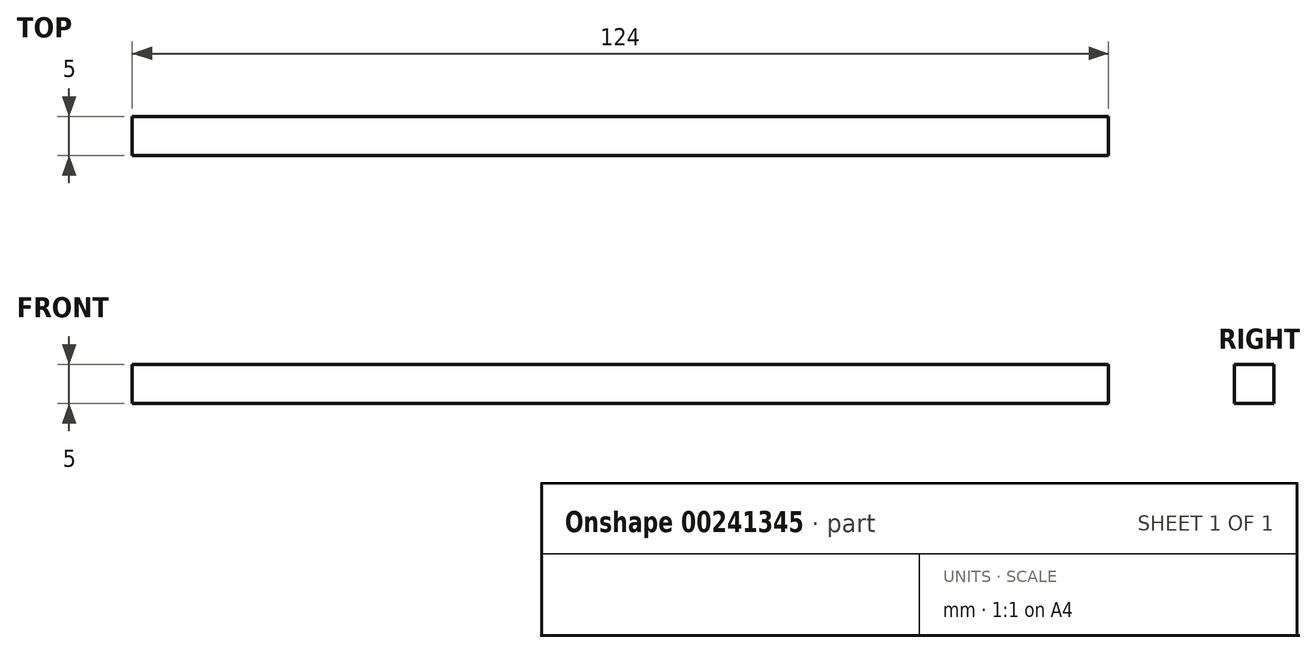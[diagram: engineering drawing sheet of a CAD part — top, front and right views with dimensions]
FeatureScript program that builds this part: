
annotation { "Feature Type Name" : "Feature", "Feature Type Description" : "" }
export const myFeature = defineFeature(function(context is Context, id is Id, definition is map)
    precondition{}
    {
        {
            var Q0;
            Q0=qCreatedBy(makeId("Right.planeOp"),FACE);
            var sketch = newSketch(context, id + "F0", { "sketchPlane" : qUnion([Q0])});
            skLineSegment(sketch, "E0.bottom", {"start": v(-2.5, 2.5) * mm, "end": v(2.5, 2.5) * mm});
            skLineSegment(sketch, "E0.top", {"start": v(-2.5, -2.5) * mm, "end": v(2.5, -2.5) * mm});
            skLineSegment(sketch, "E0.left", {"start": v(-2.5, 2.5) * mm, "end": v(-2.5, -2.5) * mm});
            skLineSegment(sketch, "E0.right", {"start": v(2.5, 2.5) * mm, "end": v(2.5, -2.5) * mm});
            skPoint(sketch, "E0.middle", {"position": v(0, 0) * mm});
            skSolve(sketch);
        }
        {
            var Q0;
            Q0 = qSketchRegion(id + "F0", true);
            extrude(context, id + "F1", {"entities" : qUnion([Q0]), "depth" : 124 * mm, "offsetDistance" : 25 * mm});
        }
    });
